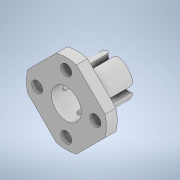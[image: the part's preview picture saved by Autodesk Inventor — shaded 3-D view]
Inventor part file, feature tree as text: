
AUTODESK INVENTOR PART (.ipt)
format: ipt  version: 2020 (Build 240168000, 168)  size: 238,592 bytes
history: native  units: in
note: dims shown in document units (in); Inventor stores cm internally (conversion verified against a paired STEP export)
features: reference x6, extrude x5, sketch x5, other x4, fillet x2, projected_geometry x2
ambient origin geometry x8: Origin, YZ Plane, XZ Plane, XY Plane, X Axis, Y Axis, Z Axis, Center Point
bodies: Solid1 (feature_tree)
feature tree (24):
  extrude  "Extrusion1"  Depth=0.4331in
  extrude  "Extrusion2"  Depth=0.3937in
  extrude  "Extrusion3"  Depth=0.1181in TaperAngle=0.0deg
  extrude  "Extrusion4"  Depth=1.1811in
  fillet  "Fillet1"  Radius=1.1811in
  fillet  "Fillet2"  Radius=0.0591in
  extrude  "Extrusion5"  Depth=0.0394in
  sketch  "Sketch1"  dims[d0=0.3228in d1=0.4331in]
  reference  "Reference1"
  reference  "Reference2"
  sketch  "Sketch2"  dims[d2=0.3937in d3=0.0in d4=0.8661in]
  sketch  "Sketch3"  dims[d5=0.1181in d6=0.0in d7=0.1575in d8=0.0in]
  reference  "Reference3"
  reference  "Reference4"
  reference  "Reference5"
  reference  "Reference6"
  sketch  "Sketch4"  dims[d9=0.0591in d10=1.1811in d11=1.1811in d12=0.0591in]
  projected_geometry  "Projected Loop1"
  sketch  "Sketch5"  dims[d13=0.3937in d14=0.0in d15=0.0394in d16=0.0394in d17=0.748in d18=135.0deg d19=0.748in d20=0.3937in d21=0.0in]
  projected_geometry  "Projected Loop2"
  parser-record x1  (decoder bookkeeping rows leaked as tree rows — omitted from the tree; the rows remain in map.json)
  other  "arm_shift_1.iam"
  other  "pin_8_45:1"
  other  "120teeth gt2 pulley:1"
note: 1 file-system path scrubbed to <path> (originals preserved in map.json)
